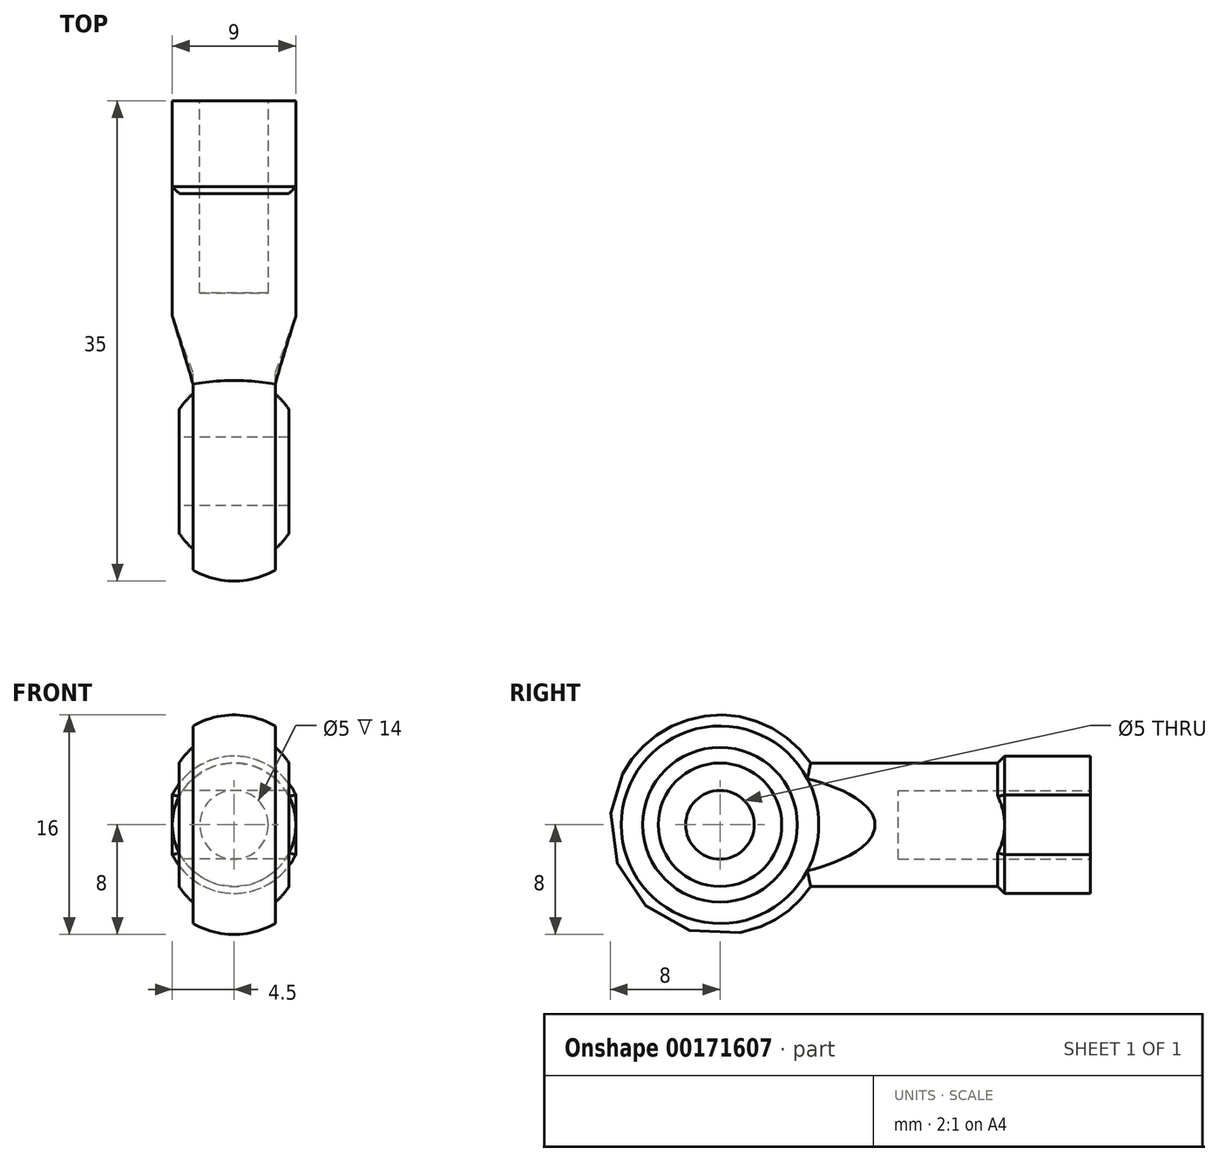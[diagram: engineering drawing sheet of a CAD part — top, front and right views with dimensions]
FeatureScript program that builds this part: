
annotation { "Feature Type Name" : "Feature", "Feature Type Description" : "" }
export const myFeature = defineFeature(function(context is Context, id is Id, definition is map)
    precondition{}
    {
        {
            assignVariable(context, id + "F0", {"name" : "B", "anyValue" : 5});
        }
        {
            assignVariable(context, id + "F1", {"name" : "L1", "anyValue" : 27});
        }
        {
            assignVariable(context, id + "F2", {"name" : "L2", "anyValue" : 14});
        }
        {
            assignVariable(context, id + "F3", {"name" : "AF", "anyValue" : 9});
        }
        {
            assignVariable(context, id + "F4", {"name" : "Wrench_Diam", "anyValue" : getVariable(context, 'AF') + 1});
        }
        {
            assignVariable(context, id + "F5", {"name" : "Chamfer_Size", "anyValue" : (getVariable(context, 'Wrench_Diam') - getVariable(context, 'AF')) / 2});
        }
        {
            var Q0;
            Q0=qCreatedBy(makeId("Top.planeOp"),FACE);
            var sketch = newSketch(context, id + "F6", { "sketchPlane" : qUnion([Q0])});
            skLineSegment(sketch, "E0", {"start": v(-4, 0) * mm, "end": v(4, 0) * mm, "construction": true});
            skLineSegment(sketch, "E1", {"start": v(-4, 2.5) * mm, "end": v(-4, 4.5) * mm});
            skArc(sketch, "E2", {"start": v(4, 4.5) * mm, "mid": v(0, 6.72) * mm, "end": v(-4, 4.5) * mm});
            skLineSegment(sketch, "E3", {"start": v(-4, 2.5) * mm, "end": v(4, 2.5) * mm});
            skLineSegment(sketch, "E4", {"start": v(4, 2.5) * mm, "end": v(4, 4.5) * mm});
            skLineSegment(sketch, "E5", {"start": v(-3, 5.64) * mm, "end": v(-3, 7.2) * mm});
            skArc(sketch, "E6", {"start": v(3, 7.2) * mm, "mid": v(0, 8) * mm, "end": v(-3, 7.2) * mm});
            skLineSegment(sketch, "E7", {"start": v(3, 7.2) * mm, "end": v(3, 5.64) * mm});
            skPoint(sketch, "E8.endSnap0", {"position": v(0, 6.72) * mm});
            skLineSegment(sketch, "E9", {"start": v(0, 0) * mm, "end": v(0, 8) * mm, "construction": true});
            skLineSegment(sketch, "E10", {"start": v(3, 7.2) * mm, "end": v(6.2, 16) * mm});
            skLineSegment(sketch, "E11", {"start": v(6, 16) * mm, "end": v(6.2, 16) * mm});
            skLineSegment(sketch, "E12", {"start": v(6, 16) * mm, "end": v(6, 2.5) * mm});
            skLineSegment(sketch, "E13", {"start": v(6, 2.5) * mm, "end": v(4, 2.5) * mm});
            skLineSegment(sketch, "E14.MirrorCS", {"start": v(-3, 7.2) * mm, "end": v(-6.2, 16) * mm});
            skLineSegment(sketch, "E15.MirrorCS", {"start": v(-6, 16) * mm, "end": v(-6.2, 16) * mm});
            skLineSegment(sketch, "E16.MirrorCS", {"start": v(-6, 16) * mm, "end": v(-6, 2.5) * mm});
            skLineSegment(sketch, "E17.MirrorCS", {"start": v(-6, 2.5) * mm, "end": v(-4, 2.5) * mm});
            skSolve(sketch);
        }
        {
            var Q0;
            {var subQ1=sQuery(id+"F6.wireOp",EDGE,"E1");Q0=makeQuery(id+"F6.imprint","IMPRINT",FACE,{"disambiguationData":[TD([[makeQuery(id+"F6.imprint","IMPRINT",EDGE,{"derivedFrom":subQ1}),-1.0]])]});}
            var Q1;
            {var subQ0=sQuery(id+"F6.wireOp",EDGE,"E5");Q1=makeQuery(id+"F6.imprint","IMPRINT",FACE,{"disambiguationData":[TD([[makeQuery(id+"F6.imprint","IMPRINT",EDGE,{"derivedFrom":subQ0}),-1.0]])]});}
            var Q2;
            Q2=sQuery(id+"F6.wireOp",EDGE,"E0");
            revolve(context, id + "F7", {"entities" : qUnion([Q0, Q1]), "axis" : qUnion([Q2]), "revolveType" : RevolveType.FULL});
        }
        {
            var Q0;
            Q0=qCreatedBy(makeId("Front.planeOp"),FACE);
            cPlane(context, id + "F8", {"entities" : qUnion([Q0]), "cplaneType" : CPlaneType.OFFSET, "offset" : (getVariable(context, 'L1')) * mm, "oppositeDirection" : true, "width" : 150 * mm, "height" : 150 * mm});
        }
        {
            var Q0;
            Q0=qCreatedBy(id+"F8.planeOp",FACE);
            var sketch = newSketch(context, id + "F9", { "sketchPlane" : qUnion([Q0])});
            skCircle(sketch, "E18", {"center": v(0, 0) * mm, "radius": 4.5 * mm});
            skArc(sketch, "E19", {"start": v(4.5, 2.18) * mm, "mid": v(0, 5) * mm, "end": v(-4.5, 2.18) * mm});
            skCircle(sketch, "E20", {"center": v(0, 0) * mm, "radius": 2.5 * mm});
            skLineSegment(sketch, "E21", {"start": v(4.5, -2.18) * mm, "end": v(4.5, 2.18) * mm});
            skLineSegment(sketch, "E22", {"start": v(-4.5, -2.18) * mm, "end": v(-4.5, 2.18) * mm});
            skArc(sketch, "E23.trimOffspring", {"start": v(-4.5, -2.18) * mm, "mid": v(0, -5) * mm, "end": v(4.5, -2.18) * mm});
            skArc(sketch, "E24", {"start": v(-4.5, 2.18) * mm, "mid": v(-5, 0) * mm, "end": v(-4.5, -2.18) * mm, "construction": true});
            skSolve(sketch);
        }
        {
            var Q0;
            Q0=makeQuery(id+"F9.imprint","IMPRINT",FACE,{"disambiguationData":[TD([[makeQuery(id+"F9.imprint","IMPRINT",EDGE,{"derivedFrom":sQuery(id+"F9.wireOp",EDGE,"E20")}),-1.0]])]});
            var Q1;
            Q1=makeQuery(id+"F9.imprint","IMPRINT",FACE,{"disambiguationData":[TD([[makeQuery(id+"F9.imprint","IMPRINT",EDGE,{"derivedFrom":sQuery(id+"F9.wireOp",EDGE,"E20")}),1.0]])]});
            extrude(context, id + "F10", {"entities" : qUnion([Q0, Q1]), "operationType" : NewBodyOperationType.ADD, "depth" : (getVariable(context, 'L1') - getVariable(context, 'B') / 2) * mm});
        }
        {
            var Q0;
            {var subQ5=sQuery(id+"F9.wireOp",EDGE,"E19");Q0=makeQuery(id+"F9.imprint","IMPRINT",FACE,{"disambiguationData":[TD([[makeQuery(id+"F9.imprint","IMPRINT",EDGE,{"derivedFrom":subQ5}),1.0]])]});}
            var Q1;
            {var subQ5=sQuery(id+"F9.wireOp",EDGE,"E23.trimOffspring");Q1=makeQuery(id+"F9.imprint","IMPRINT",FACE,{"disambiguationData":[TD([[makeQuery(id+"F9.imprint","IMPRINT",EDGE,{"derivedFrom":subQ5}),1.0]])]});}
            extrude(context, id + "F11", {"entities" : qUnion([Q0, Q1]), "operationType" : NewBodyOperationType.ADD, "depth" : (getVariable(context, 'L1') / 4) * mm});
        }
        {
            var Q0;
            Q0=makeQuery(id+"F9.imprint","IMPRINT",FACE,{"disambiguationData":[TD([[makeQuery(id+"F9.imprint","IMPRINT",EDGE,{"derivedFrom":sQuery(id+"F9.wireOp",EDGE,"E20")}),1.0]])]});
            extrude(context, id + "F12", {"entities" : qUnion([Q0]), "operationType" : NewBodyOperationType.REMOVE, "depth" : (getVariable(context, 'L2')) * mm});
        }
        {
            var Q0;
            Q0=makeQuery(id+"F11.opExtrude","CAP_EDGE",EDGE,{"disambiguationData":[OSD([sQuery(id+"F9.wireOp",EDGE,"E19")])],"isStart":false});
            var Q1;
            {var subQ0=sQuery(id+"F9.wireOp",EDGE,"E21");Q1=makeQuery(id+"F11.opExtrude","CAP_EDGE",EDGE,{"disambiguationData":[OSD([subQ0]),TDD([makeQuery(id+"F9.imprint","IMPRINT",EDGE,{"disambiguationData":[TD([[makeQuery(id+"F9.imprint","INTERSECT",VERTEX,{"derivedFrom":[sQuery(id+"F9.wireOp",EDGE,"E19"),subQ0]}),1.0]])],"derivedFrom":subQ0})])],"isStart":false});}
            var Q2;
            {var subQ0=sQuery(id+"F9.wireOp",EDGE,"E22");Q2=makeQuery(id+"F11.opExtrude","CAP_EDGE",EDGE,{"disambiguationData":[OSD([subQ0]),TDD([makeQuery(id+"F9.imprint","IMPRINT",EDGE,{"disambiguationData":[TD([[makeQuery(id+"F9.imprint","INTERSECT",VERTEX,{"derivedFrom":[sQuery(id+"F9.wireOp",EDGE,"E19"),subQ0]}),1.0]])],"derivedFrom":subQ0})])],"isStart":false});}
            var Q3;
            Q3=makeQuery(id+"F11.opExtrude","CAP_EDGE",EDGE,{"disambiguationData":[OSD([sQuery(id+"F9.wireOp",EDGE,"E23.trimOffspring")])],"isStart":false});
            var Q4;
            {var subQ0=sQuery(id+"F9.wireOp",EDGE,"E21");Q4=makeQuery(id+"F11.opExtrude","CAP_EDGE",EDGE,{"disambiguationData":[OSD([subQ0]),TDD([makeQuery(id+"F9.imprint","IMPRINT",EDGE,{"disambiguationData":[TD([[makeQuery(id+"F9.imprint","INTERSECT",VERTEX,{"derivedFrom":[subQ0,sQuery(id+"F9.wireOp",EDGE,"E23.trimOffspring")]}),-1.0]])],"derivedFrom":subQ0})])],"isStart":false});}
            var Q5;
            {var subQ0=sQuery(id+"F9.wireOp",EDGE,"E22");Q5=makeQuery(id+"F11.opExtrude","CAP_EDGE",EDGE,{"disambiguationData":[OSD([subQ0]),TDD([makeQuery(id+"F9.imprint","IMPRINT",EDGE,{"disambiguationData":[TD([[makeQuery(id+"F9.imprint","INTERSECT",VERTEX,{"derivedFrom":[subQ0,sQuery(id+"F9.wireOp",EDGE,"E23.trimOffspring")]}),-1.0]])],"derivedFrom":subQ0})])],"isStart":false});}
            chamfer(context, id + "F13", {"entities" : qUnion([Q0, Q1, Q2, Q3, Q4, Q5]), "width" : (getVariable(context, 'Chamfer_Size')) * mm, "tangentPropagation" : true});
        }
        {
            var Q0;
            {var subQ1=sQuery(id+"F6.wireOp",EDGE,"E4");Q0=makeQuery(id+"F6.imprint","IMPRINT",FACE,{"disambiguationData":[TD([[makeQuery(id+"F6.imprint","IMPRINT",EDGE,{"derivedFrom":subQ1}),-1.0]])]});}
            var Q1;
            {var subQ2=sQuery(id+"F6.wireOp",EDGE,"E1");Q1=makeQuery(id+"F6.imprint","IMPRINT",FACE,{"disambiguationData":[TD([[makeQuery(id+"F6.imprint","IMPRINT",EDGE,{"derivedFrom":subQ2}),1.0]])]});}
            var Q2;
            Q2=sQuery(id+"F6.wireOp",EDGE,"E0");
            revolve(context, id + "F14", {"operationType" : NewBodyOperationType.REMOVE, "entities" : qUnion([Q0, Q1]), "axis" : qUnion([Q2]), "revolveType" : RevolveType.FULL, "oppositeDirection" : true});
        }
    });
